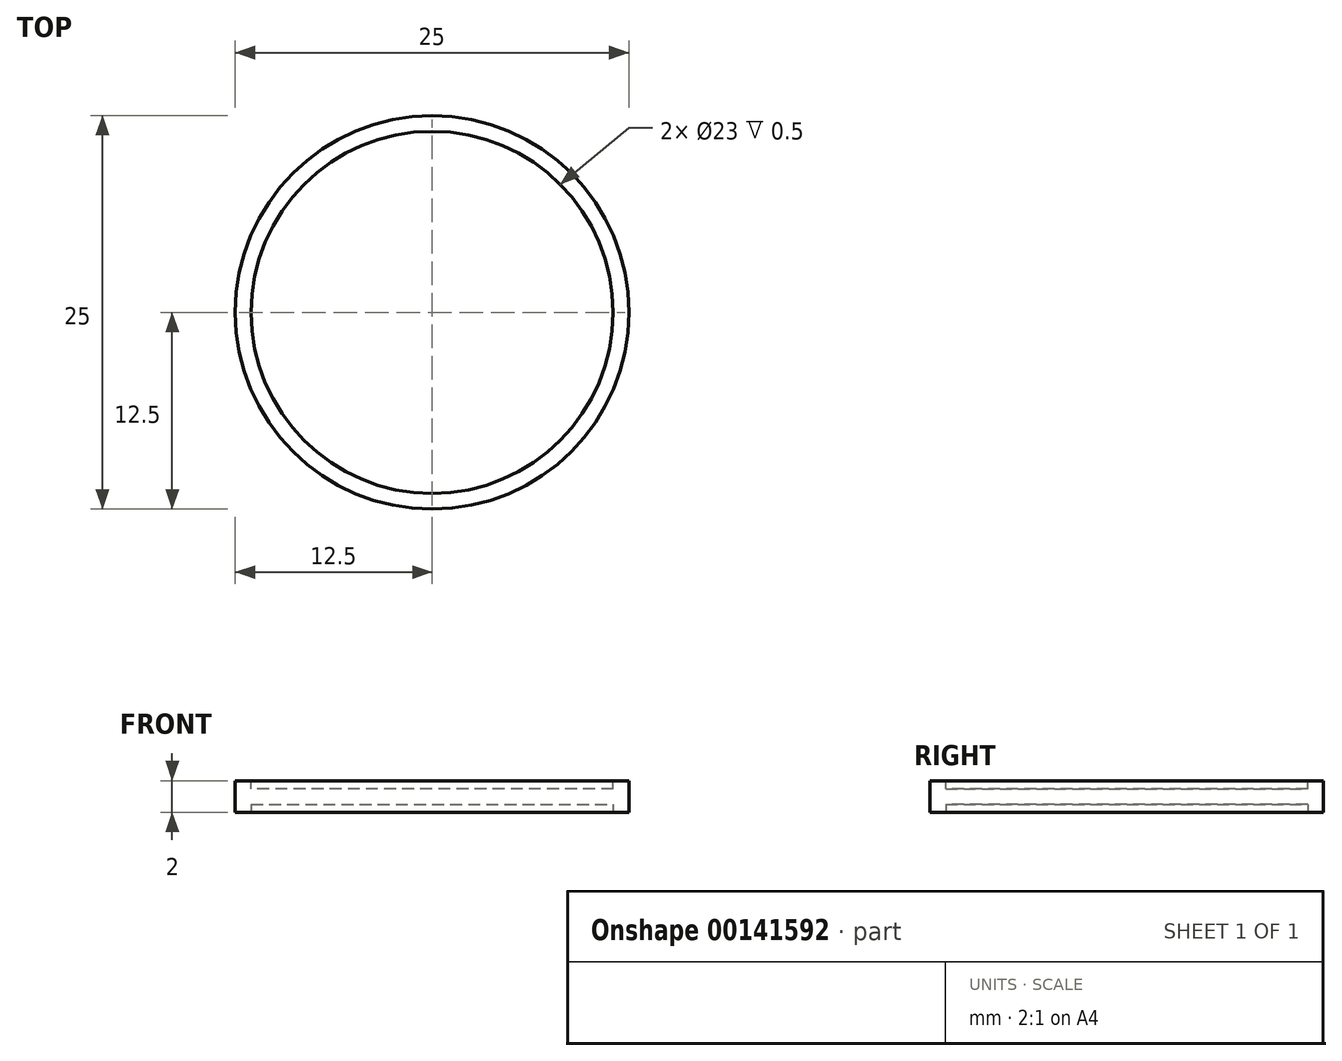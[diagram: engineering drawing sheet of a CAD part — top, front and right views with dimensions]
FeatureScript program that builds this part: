
annotation { "Feature Type Name" : "Feature", "Feature Type Description" : "" }
export const myFeature = defineFeature(function(context is Context, id is Id, definition is map)
    precondition{}
    {
        {
            assignVariable(context, id + "F0", {"name" : "ImpressionDepth", "anyValue" : 0.5});
        }
        {
            var Q0;
            Q0=qCreatedBy(makeId("Top.planeOp"),FACE);
            var sketch = newSketch(context, id + "F1", { "sketchPlane" : qUnion([Q0])});
            skCircle(sketch, "E0", {"center": v(0, 0) * mm, "radius": 12.5 * mm});
            skSolve(sketch);
        }
        {
            var Q0;
            Q0 = qSketchRegion(id + "F1", true);
            extrude(context, id + "F2", {"entities" : qUnion([Q0]), "depth" : 2 * mm});
        }
        {
            var Q0;
            Q0=makeQuery(id+"F2.opExtrude","CAP_FACE",FACE,{"disambiguationData":[OSD([sQuery(id+"F1.wireOp",EDGE,"E0")])],"isStart":false});
            var sketch = newSketch(context, id + "F3", { "sketchPlane" : qUnion([Q0])});
            skCircle(sketch, "E1.0", {"center": v(0, 0) * mm, "radius": 11.5 * mm});
            skSolve(sketch);
        }
        {
            var Q0;
            Q0 = qSketchRegion(id + "F3", true);
            extrude(context, id + "F4", {"entities" : qUnion([Q0]), "operationType" : NewBodyOperationType.REMOVE, "oppositeDirection" : true, "depth" : (getVariable(context, 'ImpressionDepth')) * mm});
        }
        {
            var Q0;
            Q0=makeQuery(id+"F2.opExtrude","CAP_FACE",FACE,{"disambiguationData":[OSD([sQuery(id+"F1.wireOp",EDGE,"E0")])],"isStart":true});
            var sketch = newSketch(context, id + "F5", { "sketchPlane" : qUnion([Q0])});
            skCircle(sketch, "E2.0", {"center": v(0, 0) * mm, "radius": 11.5 * mm});
            skSolve(sketch);
        }
        {
            var Q0;
            Q0 = qSketchRegion(id + "F5", true);
            extrude(context, id + "F6", {"entities" : qUnion([Q0]), "operationType" : NewBodyOperationType.REMOVE, "oppositeDirection" : true, "depth" : (getVariable(context, 'ImpressionDepth')) * mm});
        }
    });
